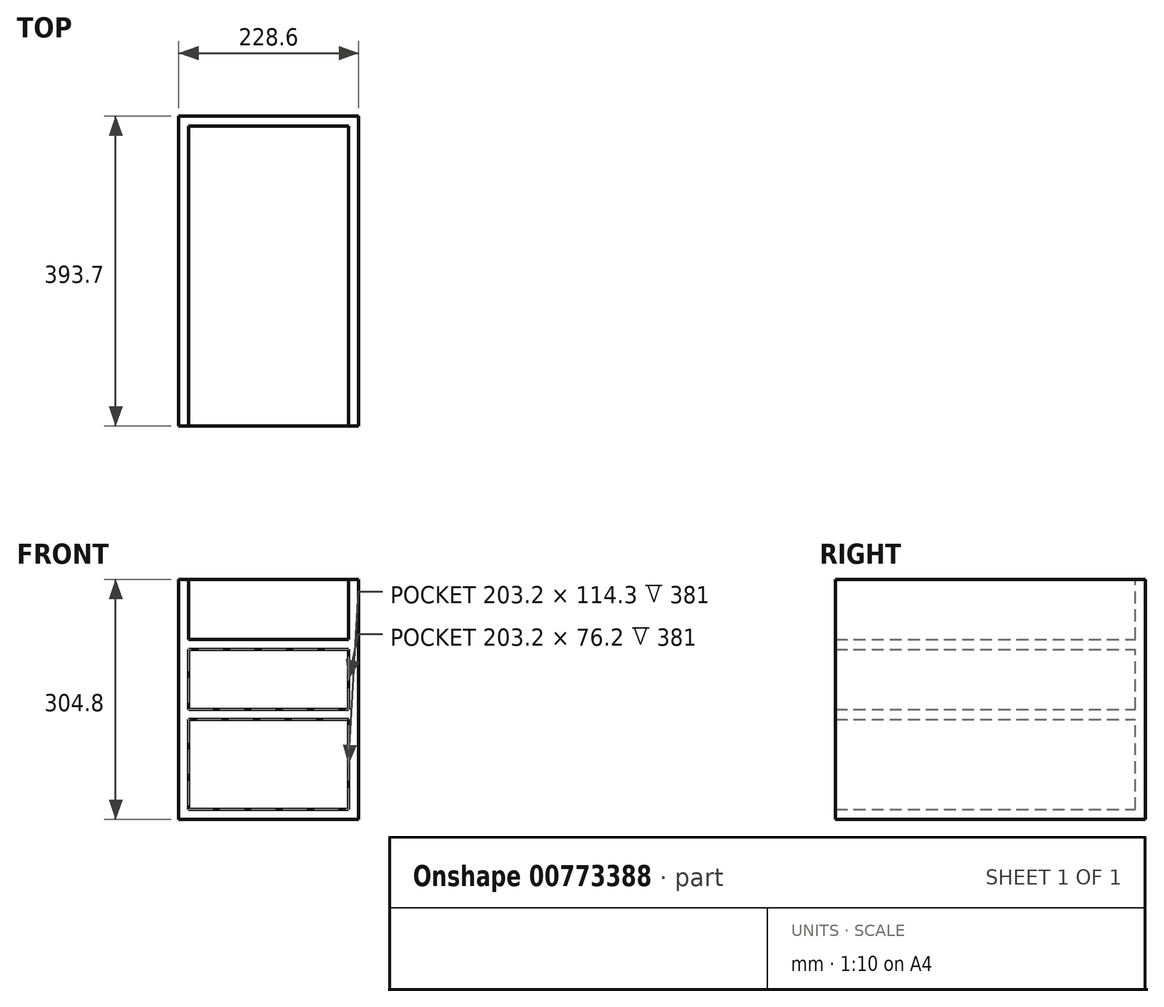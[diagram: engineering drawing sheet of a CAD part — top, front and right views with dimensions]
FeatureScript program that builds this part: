
annotation { "Feature Type Name" : "Feature", "Feature Type Description" : "" }
export const myFeature = defineFeature(function(context is Context, id is Id, definition is map)
    precondition{}
    {
        {
            var Q0;
            Q0=qCreatedBy(makeId("Top.planeOp"),FACE);
            var sketch = newSketch(context, id + "F0", { "sketchPlane" : qUnion([Q0])});
            skLineSegment(sketch, "E0.bottom", {"start": v(101.6, -190.5) * mm, "end": v(-101.6, -190.5) * mm});
            skLineSegment(sketch, "E0.top", {"start": v(101.6, 190.5) * mm, "end": v(-101.6, 190.5) * mm});
            skLineSegment(sketch, "E0.left", {"start": v(101.6, -190.5) * mm, "end": v(101.6, 190.5) * mm});
            skLineSegment(sketch, "E0.right", {"start": v(-101.6, -190.5) * mm, "end": v(-101.6, 190.5) * mm});
            skPoint(sketch, "E0.middle", {"position": v(0, 0) * mm});
            skSolve(sketch);
        }
        {
            var Q0;
            Q0=makeQuery(id+"F0.imprint","IMPRINT",FACE,{"disambiguationData":[TD([[makeQuery(id+"F0.imprint","IMPRINT",EDGE,{"derivedFrom":sQuery(id+"F0.wireOp",EDGE,"E0.bottom")}),-1.0]])]});
            extrude(context, id + "F1", {"entities" : qUnion([Q0]), "depth" : 12.7 * mm, "offsetDistance" : 25.4 * mm});
        }
        {
            var Q0;
            Q0=makeQuery(id+"F1.opExtrude","SWEPT_FACE",FACE,{"disambiguationData":[OSD([sQuery(id+"F0.wireOp",EDGE,"E0.top")])]});
            var sketch = newSketch(context, id + "F2", { "sketchPlane" : qUnion([Q0])});
            skLineSegment(sketch, "E1.bottom", {"start": v(-101.6, 0) * mm, "end": v(101.6, 0) * mm});
            skLineSegment(sketch, "E1.top", {"start": v(-101.6, 304.8) * mm, "end": v(101.6, 304.8) * mm});
            skLineSegment(sketch, "E1.left", {"start": v(-101.6, 0) * mm, "end": v(-101.6, 304.8) * mm});
            skLineSegment(sketch, "E1.right", {"start": v(101.6, 0) * mm, "end": v(101.6, 304.8) * mm});
            skSolve(sketch);
        }
        {
            var Q0;
            {var subQ0=sQuery(id+"F2.wireOp",EDGE,"E1.top");Q0=makeQuery(id+"F2.imprint","IMPRINT",FACE,{"disambiguationData":[TD([[makeQuery(id+"F2.imprint","IMPRINT",EDGE,{"derivedFrom":subQ0}),-1.0]])]});}
            var Q1;
            {var subQ0=sQuery(id+"F2.wireOp",EDGE,"E1.bottom");Q1=makeQuery(id+"F2.imprint","IMPRINT",FACE,{"disambiguationData":[TD([[makeQuery(id+"F2.imprint","IMPRINT",EDGE,{"derivedFrom":subQ0}),1.0]])]});}
            extrude(context, id + "F3", {"entities" : qUnion([Q0, Q1]), "operationType" : NewBodyOperationType.ADD, "depth" : 12.7 * mm, "offsetDistance" : 25.4 * mm});
        }
        {
            var Q0;
            Q0=makeQuery(id+"F3.boolean.opBoolean","MERGE",FACE,{"derivedFrom":[makeQuery(id+"F1.opExtrude","SWEPT_FACE",FACE,{"disambiguationData":[OSD([sQuery(id+"F0.wireOp",EDGE,"E0.left")])]}),makeQuery(id+"F3.opExtrude","SWEPT_FACE",FACE,{"disambiguationData":[OSD([sQuery(id+"F2.wireOp",EDGE,"E1.left")])]})]});
            var sketch = newSketch(context, id + "F4", { "sketchPlane" : qUnion([Q0])});
            skLineSegment(sketch, "E2.bottom", {"start": v(203.2, 0) * mm, "end": v(-190.5, 0) * mm});
            skLineSegment(sketch, "E2.top", {"start": v(203.2, 304.8) * mm, "end": v(-190.5, 304.8) * mm});
            skLineSegment(sketch, "E2.left", {"start": v(203.2, 0) * mm, "end": v(203.2, 304.8) * mm});
            skLineSegment(sketch, "E2.right", {"start": v(-190.5, 0) * mm, "end": v(-190.5, 304.8) * mm});
            skSolve(sketch);
        }
        {
            var Q0;
            {var subQ4=makeQuery(id+"F1.opExtrude","CAP_EDGE",EDGE,{"disambiguationData":[OSD([sQuery(id+"F0.wireOp",EDGE,"E0.left")])],"isStart":false});Q0=makeQuery(id+"F4.imprint","IMPRINT",FACE,{"disambiguationData":[TD([[makeQuery(id+"F4.imprint","IMPRINT",EDGE,{"derivedFrom":subQ4}),1.0]])]});}
            var Q1;
            {var subQ4=sQuery(id+"F4.wireOp",EDGE,"E2.bottom");Q1=makeQuery(id+"F4.imprint","IMPRINT",FACE,{"disambiguationData":[TD([[makeQuery(id+"F4.imprint","IMPRINT",EDGE,{"derivedFrom":subQ4}),1.0]])]});}
            extrude(context, id + "F5", {"entities" : qUnion([Q0, Q1]), "operationType" : NewBodyOperationType.ADD, "depth" : 12.7 * mm, "offsetDistance" : 25.4 * mm});
        }
        {
            var Q0;
            Q0=makeQuery(id+"F3.boolean.opBoolean","MERGE",FACE,{"derivedFrom":[makeQuery(id+"F1.opExtrude","SWEPT_FACE",FACE,{"disambiguationData":[OSD([sQuery(id+"F0.wireOp",EDGE,"E0.right")])]}),makeQuery(id+"F3.opExtrude","SWEPT_FACE",FACE,{"disambiguationData":[OSD([sQuery(id+"F2.wireOp",EDGE,"E1.right")])]})]});
            var sketch = newSketch(context, id + "F6", { "sketchPlane" : qUnion([Q0])});
            skLineSegment(sketch, "E3.bottom", {"start": v(-203.2, 0) * mm, "end": v(190.5, 0) * mm});
            skLineSegment(sketch, "E3.top", {"start": v(-203.2, 304.8) * mm, "end": v(190.5, 304.8) * mm});
            skLineSegment(sketch, "E3.left", {"start": v(-203.2, 0) * mm, "end": v(-203.2, 304.8) * mm});
            skLineSegment(sketch, "E3.right", {"start": v(190.5, 0) * mm, "end": v(190.5, 304.8) * mm});
            skSolve(sketch);
        }
        {
            var Q0;
            {var subQ4=sQuery(id+"F6.wireOp",EDGE,"E3.bottom");Q0=makeQuery(id+"F6.imprint","IMPRINT",FACE,{"disambiguationData":[TD([[makeQuery(id+"F6.imprint","IMPRINT",EDGE,{"derivedFrom":subQ4}),-1.0]])]});}
            var Q1;
            {var subQ4=makeQuery(id+"F1.opExtrude","CAP_EDGE",EDGE,{"disambiguationData":[OSD([sQuery(id+"F0.wireOp",EDGE,"E0.right")])],"isStart":false});Q1=makeQuery(id+"F6.imprint","IMPRINT",FACE,{"disambiguationData":[TD([[makeQuery(id+"F6.imprint","IMPRINT",EDGE,{"derivedFrom":subQ4}),-1.0]])]});}
            extrude(context, id + "F7", {"entities" : qUnion([Q0, Q1]), "operationType" : NewBodyOperationType.ADD, "depth" : 12.7 * mm, "offsetDistance" : 25.4 * mm});
        }
        {
            var Q0;
            Q0=makeQuery(id+"F3.opExtrude","CAP_FACE",FACE,{"disambiguationData":[OSD([sQuery(id+"F2.wireOp",EDGE,"E1.bottom"),sQuery(id+"F2.wireOp",EDGE,"E1.top"),sQuery(id+"F2.wireOp",EDGE,"E1.left"),sQuery(id+"F2.wireOp",EDGE,"E1.right")])],"isStart":true});
            var sketch = newSketch(context, id + "F8", { "sketchPlane" : qUnion([Q0])});
            skLineSegment(sketch, "E4", {"start": v(-101.6, 304.8) * mm, "end": v(-101.6, 228.6) * mm});
            skLineSegment(sketch, "E5.bottom", {"start": v(-101.6, 228.6) * mm, "end": v(101.6, 228.6) * mm});
            skLineSegment(sketch, "E5.top", {"start": v(-101.6, 215.9) * mm, "end": v(101.6, 215.9) * mm});
            skLineSegment(sketch, "E5.left", {"start": v(-101.6, 228.6) * mm, "end": v(-101.6, 215.9) * mm});
            skLineSegment(sketch, "E5.right", {"start": v(101.6, 228.6) * mm, "end": v(101.6, 215.9) * mm});
            skSolve(sketch);
        }
        {
            var Q0;
            Q0=makeQuery(id+"F8.imprint","IMPRINT",FACE,{"disambiguationData":[TD([[makeQuery(id+"F8.imprint","IMPRINT",EDGE,{"derivedFrom":sQuery(id+"F8.wireOp",EDGE,"E5.bottom")}),-1.0]])]});
            extrude(context, id + "F9", {"entities" : qUnion([Q0]), "operationType" : NewBodyOperationType.ADD, "depth" : 381 * mm, "offsetDistance" : 25.4 * mm});
        }
        {
            var Q0;
            Q0=makeQuery(id+"F9.boolean.opBoolean","SPLIT",FACE,{"disambiguationData":[TD([makeQuery(id+"F9.opExtrude","SWEPT_FACE",FACE,{"disambiguationData":[OSD([sQuery(id+"F8.wireOp",EDGE,"E5.top")])]})])],"derivedFrom":makeQuery(id+"F3.opExtrude","CAP_FACE",FACE,{"disambiguationData":[OSD([sQuery(id+"F2.wireOp",EDGE,"E1.bottom"),sQuery(id+"F2.wireOp",EDGE,"E1.top"),sQuery(id+"F2.wireOp",EDGE,"E1.left"),sQuery(id+"F2.wireOp",EDGE,"E1.right")])],"isStart":true})});
            var sketch = newSketch(context, id + "F10", { "sketchPlane" : qUnion([Q0])});
            skLineSegment(sketch, "E6", {"start": v(-101.6, 215.9) * mm, "end": v(-101.6, 139.7) * mm});
            skLineSegment(sketch, "E7.bottom", {"start": v(-101.6, 139.7) * mm, "end": v(101.6, 139.7) * mm});
            skLineSegment(sketch, "E7.top", {"start": v(-101.6, 127) * mm, "end": v(101.6, 127) * mm});
            skLineSegment(sketch, "E7.left", {"start": v(-101.6, 139.7) * mm, "end": v(-101.6, 127) * mm});
            skLineSegment(sketch, "E7.right", {"start": v(101.6, 139.7) * mm, "end": v(101.6, 127) * mm});
            skSolve(sketch);
        }
        {
            var Q0;
            Q0=makeQuery(id+"F10.imprint","IMPRINT",FACE,{"disambiguationData":[TD([[makeQuery(id+"F10.imprint","IMPRINT",EDGE,{"derivedFrom":sQuery(id+"F10.wireOp",EDGE,"E7.bottom")}),-1.0]])]});
            extrude(context, id + "F11", {"entities" : qUnion([Q0]), "operationType" : NewBodyOperationType.ADD, "depth" : 381 * mm, "offsetDistance" : 25.4 * mm});
        }
    });
